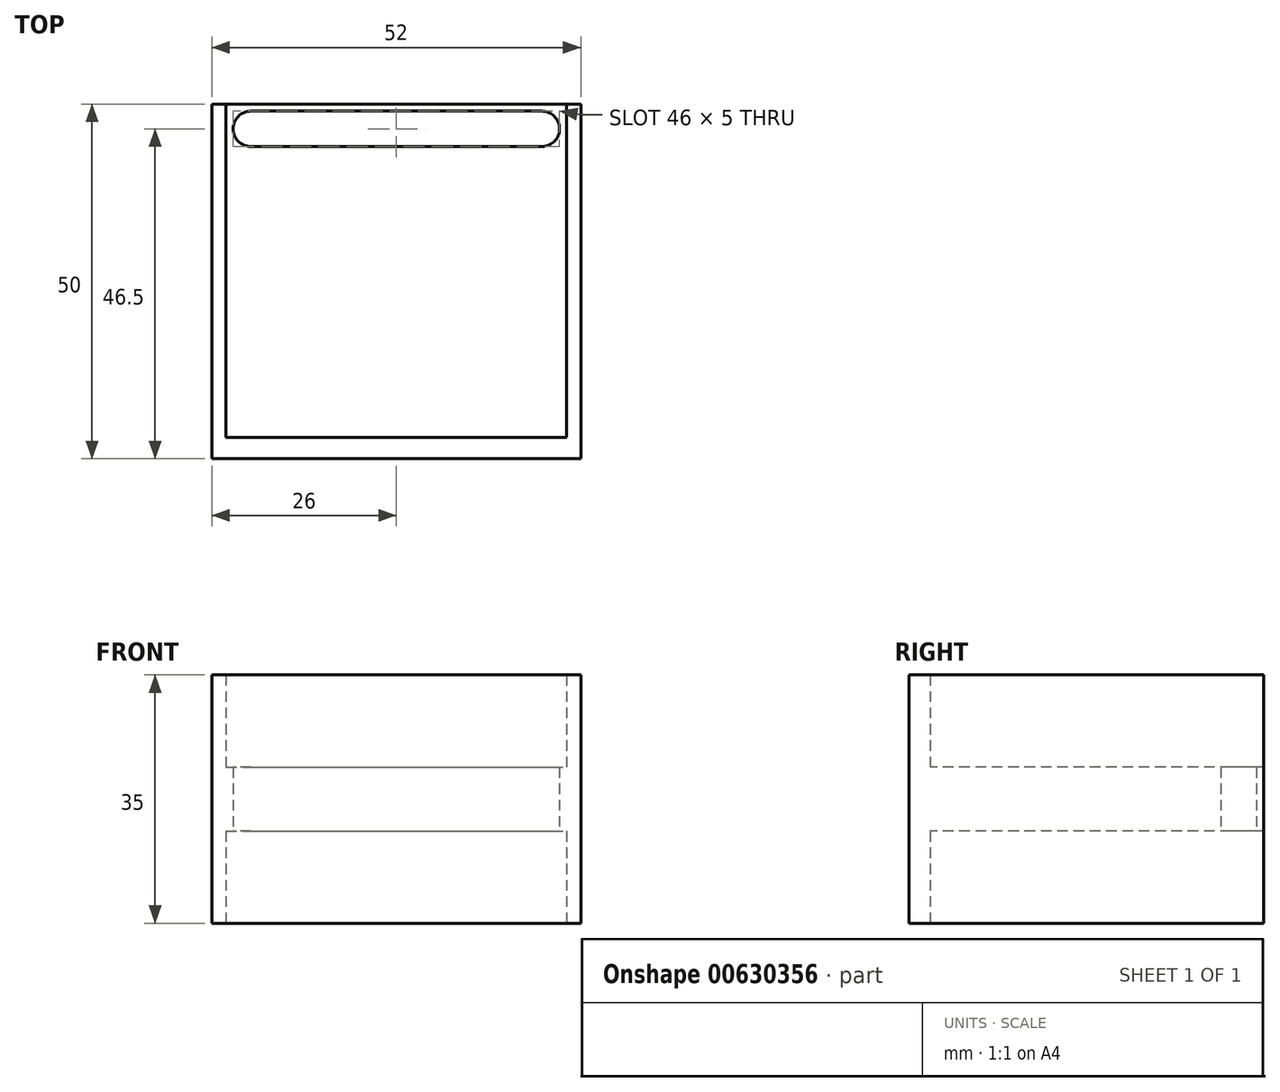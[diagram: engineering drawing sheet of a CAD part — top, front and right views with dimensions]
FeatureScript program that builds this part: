
annotation { "Feature Type Name" : "Feature", "Feature Type Description" : "" }
export const myFeature = defineFeature(function(context is Context, id is Id, definition is map)
    precondition{}
    {
        {
            var Q0;
            Q0=qCreatedBy(makeId("Top.planeOp"),FACE);
            var sketch = newSketch(context, id + "F0", { "sketchPlane" : qUnion([Q0])});
            skLineSegment(sketch, "E0.bottom", {"start": v(-26, 25) * mm, "end": v(26, 25) * mm});
            skLineSegment(sketch, "E0.top", {"start": v(-26, -25) * mm, "end": v(26, -25) * mm});
            skLineSegment(sketch, "E0.left", {"start": v(-26, 25) * mm, "end": v(-26, -25) * mm});
            skLineSegment(sketch, "E0.right", {"start": v(26, 25) * mm, "end": v(26, -25) * mm});
            skPoint(sketch, "E0.middle", {"position": v(0, 0) * mm});
            skCircle(sketch, "E1", {"center": v(-20.5, 21.5) * mm, "radius": 2.5 * mm});
            skCircle(sketch, "E2.MirrorC", {"center": v(20.5, 21.5) * mm, "radius": 2.5 * mm});
            skLineSegment(sketch, "E3", {"start": v(-24, 25) * mm, "end": v(-24, -25) * mm});
            skLineSegment(sketch, "E4", {"start": v(24, 25) * mm, "end": v(24, -25) * mm});
            skLineSegment(sketch, "E5", {"start": v(-24, -22) * mm, "end": v(24, -22) * mm});
            skLineSegment(sketch, "E6", {"start": v(-20.5, 24) * mm, "end": v(20.5, 24) * mm});
            skLineSegment(sketch, "E7", {"start": v(-20.5, 19) * mm, "end": v(20.5, 19) * mm});
            skSolve(sketch);
        }
        {
            var Q0;
            {var subQ3=sQuery(id+"F0.wireOp",EDGE,"E5");Q0=makeQuery(id+"F0.imprint","IMPRINT",FACE,{"disambiguationData":[TD([[makeQuery(id+"F0.imprint","IMPRINT",EDGE,{"derivedFrom":subQ3}),1.0]])]});}
            extrude(context, id + "F1", {"entities" : qUnion([Q0]), "endBound" : BoundingType.SYMMETRIC, "depth" : 9 * mm, "offsetDistance" : 25 * mm});
        }
        {
            var Q0;
            {var subQ4=sQuery(id+"F0.wireOp",EDGE,"E0.left");Q0=makeQuery(id+"F0.imprint","IMPRINT",FACE,{"disambiguationData":[TD([[makeQuery(id+"F0.imprint","IMPRINT",EDGE,{"derivedFrom":subQ4}),1.0]])]});}
            var Q1;
            {var subQ5=sQuery(id+"F0.wireOp",EDGE,"E5");Q1=makeQuery(id+"F0.imprint","IMPRINT",FACE,{"disambiguationData":[TD([[makeQuery(id+"F0.imprint","IMPRINT",EDGE,{"derivedFrom":subQ5}),-1.0]])]});}
            var Q2;
            {var subQ4=sQuery(id+"F0.wireOp",EDGE,"E0.right");Q2=makeQuery(id+"F0.imprint","IMPRINT",FACE,{"disambiguationData":[TD([[makeQuery(id+"F0.imprint","IMPRINT",EDGE,{"derivedFrom":subQ4}),-1.0]])]});}
            extrude(context, id + "F2", {"entities" : qUnion([Q0, Q1, Q2]), "operationType" : NewBodyOperationType.ADD, "endBound" : BoundingType.SYMMETRIC, "depth" : 35 * mm, "offsetDistance" : 25 * mm});
        }
    });
